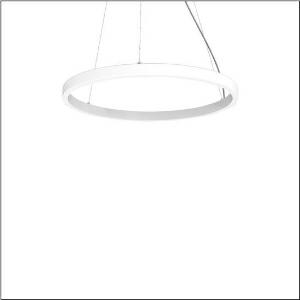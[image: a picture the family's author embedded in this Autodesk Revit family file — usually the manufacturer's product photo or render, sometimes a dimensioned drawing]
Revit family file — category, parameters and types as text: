
# Revit family: silica_r__21_ring-o_5pjbo3d3004a_bcd7
name_source: partatom
category: Lighting Fixtures
units: mm (PartAtom-declared; Revit-internal decimal feet)

## family parameters
Cut with Voids When Loaded = No
Host = Face
Light Source = No
Part Type = Normal
Room Calculation Point = No
Round Connector Dimension = Use Diameter
Shared = No

## types (1)
- Silica® 21 Ring-O (1 x LED, 7210 lm, 105 W, 4000K)
    Apparent Load = 105 VA
    CIE Flux Codes = 2 16 49 50 100
    Color Rendering = 80
    Color Temperature = 4000K
    Default Elevation = 1800 mm
    Description = Silica® 21 Ring-O, suspended luminaire, of PMMA, frosted, light emission: outer ring side luminous distribution, primary light characteristic: symmetric, installation type: suspended mounting, LED, rated luminous flux: 7.210lm, luminous efficacy: 69lm/W, light colour: 840, colour temperature: 4000K, control gear: DALI 2, with terminal, 5-pole, mains connection: 230V, AC/DC, 0/50..60Hz, rated input power: 105W, housing, of extruded aluminium section, traffic white (RAL 9016), diameter: 1.100mm, ceiling canopy, traffic white (RAL 9016), protection rating (lamp compartment): IP40, insulation class (complete): insulation class I (protective earthing), certification: CE, impact resistance: IK02, permissible operating ambient temperature: 0..+35°C, packaging unit: 1 piece
    Height = 48 mm  [stored 0.15748 ft]
    Lamp = 1 x LED
    Lamp Light Flux = 7210 lm
    Lamp Power = 105 W
    Lamp count = 1
    Length = 1100 mm
    Luminous efficacy = 69 lm/W
    Manufacturer = Siteco
    ModVariant = No
    Model = 5PJBO3D3004A
    Mounting Place = Ceiling
    Mounting Type = Pendant
    Number of Poles = 1
    OnlyDefault = Yes
    Power Factor = 1
    Product Name = Silica® 21 Ring-O
    Product group = suspended luminaire
    ProductGroupID = 905
    Protection Class = Protection class I
    Protection Degree = IP 40
    RLX_Detail_Level = 1
    RLX_Emergency_Light_Flux = 0 lm
    RLX_Emergency_Type = 0
    RLX_Emergency_Type_DB = No
    RlxData = <blob elided: 13541 chars, md5=633927b2>
    Socket = socket
    Standby Power = 0 W
    System Light Flux = 7210 lm
    System Power = 105 W
    Type Comments = Product without accessories
    Type Image = l_1258387.jpg
    URL = http://relux.com
    VarID = ---
    Voltage = 0 V
    Weight = 0.00 kg
    Width = 0 mm  [stored 0 ft]

note: [stored X ft] marks values corroborated as IEEE doubles in the binary element streams (Revit-internal decimal feet)

## geometry (parser evidence)
native form markers: Sweep x11
no freeform markers — native parametric forms only
